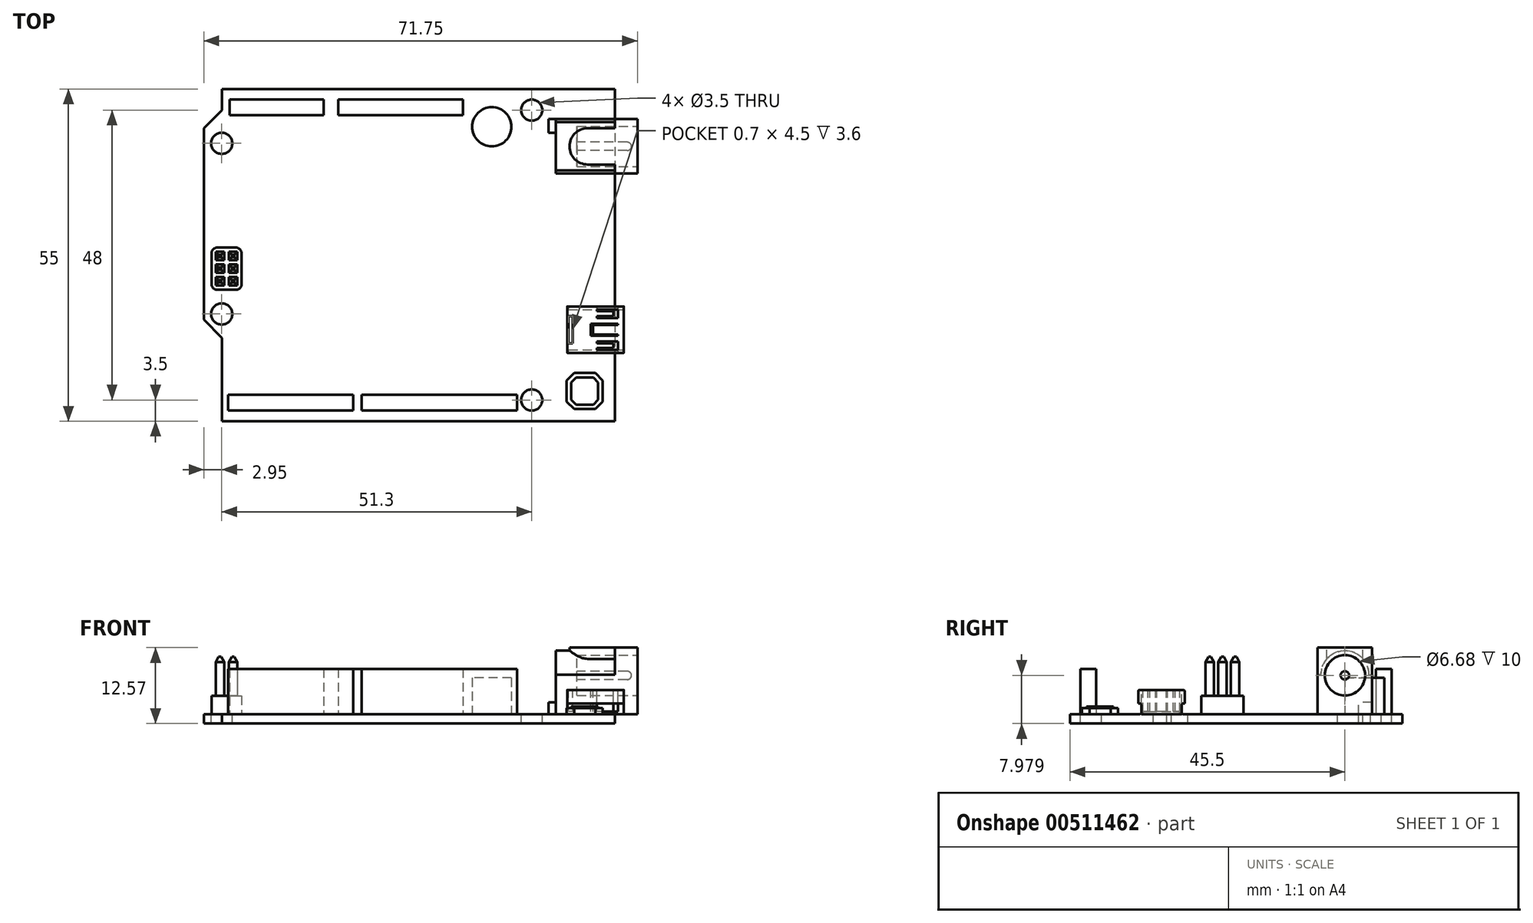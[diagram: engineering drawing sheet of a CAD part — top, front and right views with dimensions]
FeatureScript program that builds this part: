
annotation { "Feature Type Name" : "Feature", "Feature Type Description" : "" }
export const myFeature = defineFeature(function(context is Context, id is Id, definition is map)
    precondition{}
    {
        {
            var Q0;
            Q0=qCreatedBy(makeId("Top.planeOp"),FACE);
            var sketch = newSketch(context, id + "F0", { "sketchPlane" : qUnion([Q0])});
            skLineSegment(sketch, "E0.bottom", {"start": v(32.5, 27.5) * mm, "end": v(-32.5, 27.5) * mm});
            skLineSegment(sketch, "E0.top", {"start": v(32.5, -27.5) * mm, "end": v(-32.5, -27.5) * mm});
            skLineSegment(sketch, "E0.left", {"start": v(32.5, 27.5) * mm, "end": v(32.5, -27.5) * mm});
            skLineSegment(sketch, "E0.right", {"start": v(-32.5, 27.5) * mm, "end": v(-32.5, -27.5) * mm});
            skPoint(sketch, "E0.middle", {"position": v(0, 0) * mm});
            skSolve(sketch);
        }
        {
            var Q0;
            Q0=qSketchRegion(id+"F0",true);
            extrude(context, id + "F1", {"entities" : qUnion([Q0]), "depth" : 1.57 * mm, "offsetDistance" : 25 * mm});
        }
        {
            var Q0;
            Q0=makeQuery(id+"F1.opExtrude","CAP_FACE",FACE,{"disambiguationData":[OSD([sQuery(id+"F0.wireOp",EDGE,"E0.bottom"),sQuery(id+"F0.wireOp",EDGE,"E0.top"),sQuery(id+"F0.wireOp",EDGE,"E0.left"),sQuery(id+"F0.wireOp",EDGE,"E0.right")])],"isStart":false});
            var sketch = newSketch(context, id + "F2", { "sketchPlane" : qUnion([Q0])});
            skLineSegment(sketch, "E1.bottom", {"start": v(-32.5, 24) * mm, "end": v(-35.5, 24) * mm});
            skLineSegment(sketch, "E1.top", {"start": v(-32.5, -13.7) * mm, "end": v(-35.5, -13.7) * mm});
            skLineSegment(sketch, "E1.left", {"start": v(-32.5, 24) * mm, "end": v(-32.5, -13.7) * mm});
            skLineSegment(sketch, "E1.right", {"start": v(-35.5, 24) * mm, "end": v(-35.5, -13.7) * mm});
            skLineSegment(sketch, "E2", {"start": v(-32.5, 24) * mm, "end": v(-35.5, 20.99) * mm});
            skLineSegment(sketch, "E3", {"start": v(-35.5, 5.15) * mm, "end": v(-32.5, 5.15) * mm, "construction": true});
            skLineSegment(sketch, "E4.MirrorCS", {"start": v(-32.5, -13.7) * mm, "end": v(-35.5, -10.69) * mm});
            skSolve(sketch);
        }
        {
            var Q0;
            Q0=makeQuery(id+"F2.imprint","IMPRINT",FACE,{"disambiguationData":[TD([[makeQuery(id+"F2.imprint","IMPRINT",EDGE,{"derivedFrom":sQuery(id+"F2.wireOp",EDGE,"E1.left")}),-1.0]])]});
            var Q1;
            Q1=makeQuery(id+"F1.opExtrude","CAP_FACE",FACE,{"disambiguationData":[OSD([sQuery(id+"F0.wireOp",EDGE,"E0.bottom"),sQuery(id+"F0.wireOp",EDGE,"E0.top"),sQuery(id+"F0.wireOp",EDGE,"E0.left"),sQuery(id+"F0.wireOp",EDGE,"E0.right")])],"isStart":true});
            extrude(context, id + "F3", {"entities" : qUnion([Q0]), "operationType" : NewBodyOperationType.ADD, "endBound" : BoundingType.UP_TO_SURFACE, "oppositeDirection" : true, "depth" : 25 * mm, "endBoundEntityFace" : qUnion([Q1]), "offsetDistance" : 25 * mm});
        }
        {
            var Q0;
            Q0=makeQuery(id+"F3.boolean.opBoolean","MERGE",FACE,{"derivedFrom":[makeQuery(id+"F1.opExtrude","CAP_FACE",FACE,{"disambiguationData":[OSD([sQuery(id+"F0.wireOp",EDGE,"E0.bottom"),sQuery(id+"F0.wireOp",EDGE,"E0.top"),sQuery(id+"F0.wireOp",EDGE,"E0.left"),sQuery(id+"F0.wireOp",EDGE,"E0.right")])],"isStart":false}),makeQuery(id+"F3.opExtrude","CAP_FACE",FACE,{"disambiguationData":[OSD([sQuery(id+"F2.wireOp",EDGE,"E1.left"),sQuery(id+"F2.wireOp",EDGE,"E1.right"),sQuery(id+"F2.wireOp",EDGE,"E2"),sQuery(id+"F2.wireOp",EDGE,"E4.MirrorCS")])],"isStart":true})]});
            var sketch = newSketch(context, id + "F4", { "sketchPlane" : qUnion([Q0])});
            skCircle(sketch, "E5", {"center": v(-32.55, 18.5) * mm, "radius": 1.75 * mm});
            skLineSegment(sketch, "E6", {"start": v(-32.55, 18.5) * mm, "end": v(-32.55, -9.75) * mm, "construction": true});
            skCircle(sketch, "E7", {"center": v(-32.55, -9.75) * mm, "radius": 1.75 * mm});
            skCircle(sketch, "E8", {"center": v(18.75, 24) * mm, "radius": 1.75 * mm});
            skLineSegment(sketch, "E9", {"start": v(18.75, 22.25) * mm, "end": v(18.75, -22.25) * mm, "construction": true});
            skCircle(sketch, "E10", {"center": v(18.75, -24) * mm, "radius": 1.75 * mm});
            skSolve(sketch);
        }
        {
            var Q0;
            Q0=qSketchRegion(id+"F4",true);
            extrude(context, id + "F5", {"entities" : qUnion([Q0]), "operationType" : NewBodyOperationType.REMOVE, "endBound" : BoundingType.THROUGH_ALL, "oppositeDirection" : true, "depth" : 25 * mm, "offsetDistance" : 25 * mm});
        }
        {
            var Q0;
            Q0=makeQuery(id+"F1.opExtrude","SWEPT_FACE",FACE,{"disambiguationData":[OSD([sQuery(id+"F0.wireOp",EDGE,"E0.left")])]});
            var sketch = newSketch(context, id + "F6", { "sketchPlane" : qUnion([Q0])});
            skLineSegment(sketch, "E11.bottom", {"start": v(13.5, 1.57) * mm, "end": v(22.5, 1.57) * mm});
            skLineSegment(sketch, "E11.top", {"start": v(13.5, 12.57) * mm, "end": v(22.5, 12.57) * mm});
            skLineSegment(sketch, "E11.left", {"start": v(13.5, 1.57) * mm, "end": v(13.5, 12.57) * mm});
            skLineSegment(sketch, "E11.right", {"start": v(22.5, 1.57) * mm, "end": v(22.5, 12.57) * mm});
            skSolve(sketch);
        }
        {
            var Q0;
            Q0=qSketchRegion(id+"F6",true);
            extrude(context, id + "F7", {"entities" : qUnion([Q0]), "operationType" : NewBodyOperationType.ADD, "oppositeDirection" : true, "depth" : 11 * mm, "offsetDistance" : 25 * mm, "hasSecondDirection" : true, "secondDirectionOppositeDirection" : false, "secondDirectionDepth" : 3.75 * mm});
        }
        {
            var Q0;
            Q0=makeQuery(id+"F7.opExtrude","SWEPT_FACE",FACE,{"disambiguationData":[OSD([sQuery(id+"F6.wireOp",EDGE,"E11.top")])]});
            var sketch = newSketch(context, id + "F8", { "sketchPlane" : qUnion([Q0])});
            skLineSegment(sketch, "E12.bottom", {"start": v(36.25, 13.5) * mm, "end": v(32.5, 13.5) * mm});
            skLineSegment(sketch, "E12.top", {"start": v(36.25, 22.5) * mm, "end": v(32.5, 22.5) * mm});
            skLineSegment(sketch, "E12.left", {"start": v(36.25, 13.5) * mm, "end": v(36.25, 22.5) * mm});
            skLineSegment(sketch, "E12.right", {"start": v(32.5, 13.5) * mm, "end": v(32.5, 22.5) * mm});
            skLineSegment(sketch, "E13.bottom", {"start": v(32.5, 21) * mm, "end": v(25, 21) * mm});
            skLineSegment(sketch, "E13.top", {"start": v(32.5, 15) * mm, "end": v(25, 15) * mm});
            skLineSegment(sketch, "E13.left", {"start": v(32.5, 21) * mm, "end": v(32.5, 15) * mm});
            skLineSegment(sketch, "E13.right", {"start": v(25, 21) * mm, "end": v(25, 15) * mm});
            skPoint(sketch, "E14", {"position": v(32.5, 18) * mm});
            skLineSegment(sketch, "E15.0", {"start": v(32.5, 27.5) * mm, "end": v(32.5, 22.5) * mm, "construction": true});
            skPoint(sketch, "E16", {"position": v(36.25, 18) * mm});
            skArc(sketch, "E17", {"start": v(28, 21) * mm, "mid": v(25, 18) * mm, "end": v(28, 15) * mm});
            skLineSegment(sketch, "E18", {"start": v(28, 18) * mm, "end": v(25, 18) * mm, "construction": true});
            skPoint(sketch, "E19", {"position": v(25, 18) * mm});
            skLineSegment(sketch, "E20", {"start": v(28, 18) * mm, "end": v(28, 21) * mm, "construction": true});
            skSolve(sketch);
        }
        {
            var Q0;
            {var subQ11=sQuery(id+"F6.wireOp",EDGE,"E11.top");var subQ12=makeQuery(id+"F7.opExtrude","CAP_EDGE",EDGE,{"disambiguationData":[OSD([subQ11])],"isStart":false});Q0=makeQuery(id+"F8.imprint","IMPRINT",FACE,{"disambiguationData":[TD([[makeQuery(id+"F8.imprint","IMPRINT",EDGE,{"derivedFrom":subQ12}),-1.0]])]});}
            var Q1;
            {var subQ0=sQuery(id+"F8.wireOp",EDGE,"E13.right");var subQ1=sQuery(id+"F8.wireOp",EDGE,"E13.bottom");var subQ2=makeQuery(id+"F8.imprint","INTERSECT",VERTEX,{"derivedFrom":[subQ1,subQ0]});Q1=makeQuery(id+"F8.imprint","IMPRINT",FACE,{"disambiguationData":[TD([[makeQuery(id+"F8.imprint","IMPRINT",EDGE,{"disambiguationData":[TD([[subQ2,1.0]])],"derivedFrom":subQ1}),1.0]])]});}
            var Q2;
            {var subQ0=sQuery(id+"F8.wireOp",EDGE,"E13.right");var subQ1=sQuery(id+"F8.wireOp",EDGE,"E13.top");var subQ2=makeQuery(id+"F8.imprint","INTERSECT",VERTEX,{"derivedFrom":[subQ1,subQ0]});Q2=makeQuery(id+"F8.imprint","IMPRINT",FACE,{"disambiguationData":[TD([[makeQuery(id+"F8.imprint","IMPRINT",EDGE,{"disambiguationData":[TD([[subQ2,1.0]])],"derivedFrom":subQ1}),-1.0]])]});}
            extrude(context, id + "F9", {"entities" : qUnion([Q0, Q1, Q2]), "operationType" : NewBodyOperationType.REMOVE, "oppositeDirection" : true, "depth" : 4.5 * mm, "offsetDistance" : 25 * mm});
        }
        {
            var Q0;
            Q0=makeQuery(id+"F7.opExtrude","CAP_FACE",FACE,{"disambiguationData":[OSD([sQuery(id+"F6.wireOp",EDGE,"E11.bottom"),sQuery(id+"F6.wireOp",EDGE,"E11.top"),sQuery(id+"F6.wireOp",EDGE,"E11.left"),sQuery(id+"F6.wireOp",EDGE,"E11.right")])],"isStart":false});
            var sketch = newSketch(context, id + "F10", { "sketchPlane" : qUnion([Q0])});
            skCircle(sketch, "E21", {"center": v(-18, 8.07) * mm, "radius": 4 * mm});
            skPoint(sketch, "E21.centerSnap0", {"position": v(-18, 8.07) * mm});
            skSolve(sketch);
        }
        {
            var Q0;
            Q0=qSketchRegion(id+"F10",true);
            var Q1;
            {var subQ0=sQuery(id+"F8.wireOp",EDGE,"E12.right");Q1=makeQuery(id+"F9.boolean.opBoolean","COPY",FACE,{"derivedFrom":makeQuery(id+"F9.opExtrude","SWEPT_FACE",FACE,{"disambiguationData":[OSD([subQ0]),TDD([makeQuery(id+"F8.imprint","IMPRINT",EDGE,{"disambiguationData":[TD([[makeQuery(id+"F8.imprint","INTERSECT",VERTEX,{"derivedFrom":[subQ0,sQuery(id+"F8.wireOp",EDGE,"E13.top"),sQuery(id+"F8.wireOp",EDGE,"E13.left")]}),1.0]])],"derivedFrom":subQ0})])]})});}
            extrude(context, id + "F11", {"entities" : qUnion([Q0]), "operationType" : NewBodyOperationType.ADD, "endBound" : BoundingType.UP_TO_SURFACE, "oppositeDirection" : true, "depth" : 25 * mm, "endBoundEntityFace" : qUnion([Q1]), "offsetDistance" : 25 * mm});
        }
        {
            var Q0;
            Q0=makeQuery(id+"F7.opExtrude","SWEPT_FACE",FACE,{"disambiguationData":[OSD([sQuery(id+"F6.wireOp",EDGE,"E11.top")])]});
            var sketch = newSketch(context, id + "F12", { "sketchPlane" : qUnion([Q0])});
            skLineSegment(sketch, "E22.0.0", {"start": v(28, 15) * mm, "end": v(32.5, 15) * mm, "construction": true});
            skArc(sketch, "E22.0.1", {"start": v(28, 21) * mm, "mid": v(25, 18) * mm, "end": v(28, 15) * mm, "construction": true});
            skLineSegment(sketch, "E22.0.2", {"start": v(28, 21) * mm, "end": v(32.5, 21) * mm, "construction": true});
            skLineSegment(sketch, "E22.0.3", {"start": v(32.5, 21) * mm, "end": v(32.5, 22) * mm, "construction": true});
            skLineSegment(sketch, "E22.0.4", {"start": v(32.5, 22) * mm, "end": v(21.5, 22) * mm, "construction": true});
            skLineSegment(sketch, "E22.0.5", {"start": v(21.5, 22) * mm, "end": v(21.5, 14) * mm, "construction": true});
            skLineSegment(sketch, "E22.0.6", {"start": v(21.5, 14) * mm, "end": v(32.5, 14) * mm, "construction": true});
            skLineSegment(sketch, "E22.0.7", {"start": v(32.5, 14) * mm, "end": v(32.5, 15) * mm, "construction": true});
            skLineSegment(sketch, "E22.1.0", {"start": v(21.5, 22) * mm, "end": v(32.5, 22) * mm, "construction": true});
            skLineSegment(sketch, "E22.1.1", {"start": v(32.5, 22) * mm, "end": v(32.5, 22.5) * mm, "construction": true});
            skLineSegment(sketch, "E22.1.2", {"start": v(32.5, 22.5) * mm, "end": v(21.5, 22.5) * mm, "construction": true});
            skLineSegment(sketch, "E22.1.3", {"start": v(21.5, 22.5) * mm, "end": v(21.5, 22) * mm, "construction": true});
            skLineSegment(sketch, "E22.2.0", {"start": v(21.5, 14) * mm, "end": v(32.5, 14) * mm, "construction": true});
            skLineSegment(sketch, "E22.2.1", {"start": v(21.5, 14) * mm, "end": v(21.5, 13.5) * mm, "construction": true});
            skLineSegment(sketch, "E22.2.2", {"start": v(21.5, 13.5) * mm, "end": v(32.5, 13.5) * mm, "construction": true});
            skLineSegment(sketch, "E22.2.3", {"start": v(32.5, 13.5) * mm, "end": v(32.5, 14) * mm, "construction": true});
            skLineSegment(sketch, "E23.bottom", {"start": v(21.5, 20.25) * mm, "end": v(22.75, 20.25) * mm});
            skLineSegment(sketch, "E23.top", {"start": v(21.5, 13.5) * mm, "end": v(22.75, 13.5) * mm});
            skLineSegment(sketch, "E23.left", {"start": v(21.5, 20.25) * mm, "end": v(21.5, 13.5) * mm});
            skLineSegment(sketch, "E23.right", {"start": v(22.75, 20.25) * mm, "end": v(22.75, 13.5) * mm});
            skSolve(sketch);
        }
        {
            var Q0;
            Q0=qSketchRegion(id+"F12",true);
            var Q1;
            Q1=makeQuery(id+"F3.boolean.opBoolean","MERGE",FACE,{"derivedFrom":[makeQuery(id+"F1.opExtrude","CAP_FACE",FACE,{"disambiguationData":[OSD([sQuery(id+"F0.wireOp",EDGE,"E0.bottom"),sQuery(id+"F0.wireOp",EDGE,"E0.top"),sQuery(id+"F0.wireOp",EDGE,"E0.left"),sQuery(id+"F0.wireOp",EDGE,"E0.right")])],"isStart":false}),makeQuery(id+"F3.opExtrude","CAP_FACE",FACE,{"disambiguationData":[OSD([sQuery(id+"F2.wireOp",EDGE,"E1.left"),sQuery(id+"F2.wireOp",EDGE,"E1.right"),sQuery(id+"F2.wireOp",EDGE,"E2"),sQuery(id+"F2.wireOp",EDGE,"E4.MirrorCS")])],"isStart":true})]});
            var Q2;
            Q2=makeQuery(id+"F1.opExtrude","SWEPT_BODY",BODY,{"disambiguationData":[OSD([sQuery(id+"F0.wireOp",EDGE,"E0.bottom"),sQuery(id+"F0.wireOp",EDGE,"E0.top"),sQuery(id+"F0.wireOp",EDGE,"E0.left"),sQuery(id+"F0.wireOp",EDGE,"E0.right")])]});
            extrude(context, id + "F13", {"entities" : qUnion([Q0]), "operationType" : NewBodyOperationType.REMOVE, "endBound" : BoundingType.UP_TO_SURFACE, "oppositeDirection" : true, "depth" : 25 * mm, "endBoundEntityFace" : qUnion([Q1]), "endBoundEntityBody" : qUnion([Q2]), "offsetDistance" : 25 * mm});
        }
        {
            var Q0;
            {var subQ1=sQuery(id+"F8.wireOp",EDGE,"E12.right");var subQ2=sQuery(id+"F6.wireOp",EDGE,"E11.right");var subQ3=sQuery(id+"F6.wireOp",EDGE,"E11.top");var subQ4=sQuery(id+"F8.wireOp",EDGE,"E13.bottom");var subQ5=sQuery(id+"F6.wireOp",EDGE,"E11.left");Q0=makeQuery(id+"F11.boolean.opBoolean","SPLIT",FACE,{"disambiguationData":[TD([makeQuery(id+"F7.opExtrude","SWEPT_FACE",FACE,{"disambiguationData":[OSD([subQ2])]})])],"derivedFrom":makeQuery(id+"F9.boolean.opBoolean","COPY",FACE,{"derivedFrom":makeQuery(id+"F9.opExtrude","CAP_FACE",FACE,{"disambiguationData":[OSD([subQ3,subQ5,subQ2,subQ1,subQ4,sQuery(id+"F8.wireOp",EDGE,"E13.top"),sQuery(id+"F8.wireOp",EDGE,"E17")])],"isStart":false})})});}
            var sketch = newSketch(context, id + "F14", { "sketchPlane" : qUnion([Q0])});
            skLineSegment(sketch, "E24.bottom", {"start": v(21.5, 22.5) * mm, "end": v(22.75, 22.5) * mm});
            skLineSegment(sketch, "E24.top", {"start": v(21.5, 20.25) * mm, "end": v(22.75, 20.25) * mm});
            skLineSegment(sketch, "E24.left", {"start": v(21.5, 22.5) * mm, "end": v(21.5, 20.25) * mm});
            skLineSegment(sketch, "E24.right", {"start": v(22.75, 22.5) * mm, "end": v(22.75, 20.25) * mm});
            skPoint(sketch, "E25.0", {"position": v(22.75, 20.25) * mm});
            skSolve(sketch);
        }
        {
            var Q0;
            Q0=qSketchRegion(id+"F14",true);
            var Q1;
            Q1=makeQuery(id+"F1.opExtrude","SWEPT_BODY",BODY,{"disambiguationData":[OSD([sQuery(id+"F0.wireOp",EDGE,"E0.bottom"),sQuery(id+"F0.wireOp",EDGE,"E0.top"),sQuery(id+"F0.wireOp",EDGE,"E0.left"),sQuery(id+"F0.wireOp",EDGE,"E0.right")])]});
            extrude(context, id + "F15", {"entities" : qUnion([Q0]), "operationType" : NewBodyOperationType.REMOVE, "endBound" : BoundingType.THROUGH_ALL, "depth" : 25 * mm, "offsetDistance" : 25 * mm, "hasSecondDirection" : true, "secondDirectionBound" : SecondDirectionBoundingType.UP_TO_BODY, "secondDirectionOppositeDirection" : true, "secondDirectionDepth" : 25 * mm, "secondDirectionBoundEntityBody" : qUnion([Q1]), "hasSecondDirectionOffset" : true, "secondDirectionOffsetDistance" : 3.5 * mm});
        }
        {
            var Q0;
            Q0=makeQuery(id+"F7.opExtrude","CAP_FACE",FACE,{"disambiguationData":[OSD([sQuery(id+"F6.wireOp",EDGE,"E11.bottom"),sQuery(id+"F6.wireOp",EDGE,"E11.top"),sQuery(id+"F6.wireOp",EDGE,"E11.left"),sQuery(id+"F6.wireOp",EDGE,"E11.right")])],"isStart":true});
            var sketch = newSketch(context, id + "F16", { "sketchPlane" : qUnion([Q0])});
            skCircle(sketch, "E26", {"center": v(18, 7.98) * mm, "radius": 3.34 * mm});
            skPoint(sketch, "E26.centerSnap0", {"position": v(18, 12.57) * mm});
            skSolve(sketch);
        }
        {
            var Q0;
            Q0=qSketchRegion(id+"F16",true);
            extrude(context, id + "F17", {"entities" : qUnion([Q0]), "operationType" : NewBodyOperationType.REMOVE, "oppositeDirection" : true, "depth" : 10 * mm, "offsetDistance" : 25 * mm});
        }
        {
            var Q0;
            Q0=makeQuery(id+"F17.boolean.opBoolean","COPY",FACE,{"derivedFrom":makeQuery(id+"F17.opExtrude","CAP_FACE",FACE,{"disambiguationData":[OSD([sQuery(id+"F16.wireOp",EDGE,"E26")])],"isStart":false})});
            var sketch = newSketch(context, id + "F18", { "sketchPlane" : qUnion([Q0])});
            skCircle(sketch, "E27", {"center": v(18, 7.98) * mm, "radius": 0.7 * mm});
            skSolve(sketch);
        }
        {
            var Q0;
            Q0=qSketchRegion(id+"F18",true);
            var Q1;
            Q1=makeQuery(id+"F7.opExtrude","CAP_FACE",FACE,{"disambiguationData":[OSD([sQuery(id+"F6.wireOp",EDGE,"E11.bottom"),sQuery(id+"F6.wireOp",EDGE,"E11.top"),sQuery(id+"F6.wireOp",EDGE,"E11.left"),sQuery(id+"F6.wireOp",EDGE,"E11.right")])],"isStart":true});
            extrude(context, id + "F19", {"entities" : qUnion([Q0]), "operationType" : NewBodyOperationType.ADD, "endBound" : BoundingType.UP_TO_SURFACE, "depth" : 25 * mm, "endBoundEntityFace" : qUnion([Q1]), "hasOffset" : true, "offsetDistance" : 1 * mm});
        }
        {
            var Q0;
            Q0=makeQuery(id+"F19.opExtrude","CAP_EDGE",EDGE,{"disambiguationData":[OSD([sQuery(id+"F18.wireOp",EDGE,"E27")])],"isStart":false});
            fillet(context, id + "F20", {"entities" : qUnion([Q0]), "radius" : 0.7 * mm, "tangentPropagation" : true, "allowEdgeOverflow" : false});
        }
        {
            var Q0;
            Q0=makeQuery(id+"F1.opExtrude","SWEPT_FACE",FACE,{"disambiguationData":[OSD([sQuery(id+"F0.wireOp",EDGE,"E0.left")])]});
            var sketch = newSketch(context, id + "F21", { "sketchPlane" : qUnion([Q0])});
            skLineSegment(sketch, "E28.bottom", {"start": v(-16.2, 1.57) * mm, "end": v(-8.5, 1.57) * mm});
            skLineSegment(sketch, "E28.top", {"start": v(-16.2, 5.57) * mm, "end": v(-8.5, 5.57) * mm});
            skLineSegment(sketch, "E28.left", {"start": v(-16.2, 1.57) * mm, "end": v(-16.2, 5.57) * mm});
            skLineSegment(sketch, "E28.right", {"start": v(-8.5, 1.57) * mm, "end": v(-8.5, 5.57) * mm});
            skSolve(sketch);
        }
        {
            var Q0;
            Q0=makeQuery(id+"F21.imprint","IMPRINT",FACE,{"disambiguationData":[TD([[makeQuery(id+"F21.imprint","IMPRINT",EDGE,{"derivedFrom":sQuery(id+"F21.wireOp",EDGE,"E28.bottom")}),-1.0]])]});
            extrude(context, id + "F22", {"entities" : qUnion([Q0]), "operationType" : NewBodyOperationType.ADD, "oppositeDirection" : true, "depth" : (9.36 - 1.5) * mm, "offsetDistance" : 25 * mm, "hasSecondDirection" : true, "secondDirectionOppositeDirection" : false, "secondDirectionDepth" : 1.5 * mm});
        }
        {
            var Q0;
            Q0=makeQuery(id+"F3.boolean.opBoolean","MERGE",FACE,{"derivedFrom":[makeQuery(id+"F1.opExtrude","CAP_FACE",FACE,{"disambiguationData":[OSD([sQuery(id+"F0.wireOp",EDGE,"E0.bottom"),sQuery(id+"F0.wireOp",EDGE,"E0.top"),sQuery(id+"F0.wireOp",EDGE,"E0.left"),sQuery(id+"F0.wireOp",EDGE,"E0.right")])],"isStart":false}),makeQuery(id+"F3.opExtrude","CAP_FACE",FACE,{"disambiguationData":[OSD([sQuery(id+"F2.wireOp",EDGE,"E1.left"),sQuery(id+"F2.wireOp",EDGE,"E1.right"),sQuery(id+"F2.wireOp",EDGE,"E2"),sQuery(id+"F2.wireOp",EDGE,"E4.MirrorCS")])],"isStart":true})]});
            var sketch = newSketch(context, id + "F23", { "sketchPlane" : qUnion([Q0])});
            skLineSegment(sketch, "E29.bottom", {"start": v(-31.25, 25.75) * mm, "end": v(-15.65, 25.75) * mm});
            skLineSegment(sketch, "E29.top", {"start": v(-31.25, 23.15) * mm, "end": v(-15.65, 23.15) * mm});
            skLineSegment(sketch, "E29.left", {"start": v(-31.25, 25.75) * mm, "end": v(-31.25, 23.15) * mm});
            skLineSegment(sketch, "E29.right", {"start": v(-15.65, 25.75) * mm, "end": v(-15.65, 23.15) * mm});
            skLineSegment(sketch, "E30.bottom", {"start": v(-13.25, 25.75) * mm, "end": v(7.4, 25.75) * mm});
            skLineSegment(sketch, "E30.top", {"start": v(-13.25, 23.15) * mm, "end": v(7.4, 23.15) * mm});
            skLineSegment(sketch, "E30.left", {"start": v(-13.25, 25.75) * mm, "end": v(-13.25, 23.15) * mm});
            skLineSegment(sketch, "E30.right", {"start": v(7.4, 25.75) * mm, "end": v(7.4, 23.15) * mm});
            skLineSegment(sketch, "E31.bottom", {"start": v(-31.5, -23.15) * mm, "end": v(-10.8, -23.15) * mm});
            skLineSegment(sketch, "E31.top", {"start": v(-31.5, -25.75) * mm, "end": v(-10.8, -25.75) * mm});
            skLineSegment(sketch, "E31.left", {"start": v(-31.5, -23.15) * mm, "end": v(-31.5, -25.75) * mm});
            skLineSegment(sketch, "E31.right", {"start": v(-10.8, -23.15) * mm, "end": v(-10.8, -25.75) * mm});
            skLineSegment(sketch, "E32.bottom", {"start": v(-9.4, -23.15) * mm, "end": v(16.35, -23.15) * mm});
            skLineSegment(sketch, "E32.top", {"start": v(-9.4, -25.75) * mm, "end": v(16.35, -25.75) * mm});
            skLineSegment(sketch, "E32.left", {"start": v(-9.4, -23.15) * mm, "end": v(-9.4, -25.75) * mm});
            skLineSegment(sketch, "E32.right", {"start": v(16.35, -23.15) * mm, "end": v(16.35, -25.75) * mm});
            skSolve(sketch);
        }
        {
            var Q0;
            Q0=qSketchRegion(id+"F23",true);
            extrude(context, id + "F24", {"entities" : qUnion([Q0]), "operationType" : NewBodyOperationType.ADD, "depth" : 7.5 * mm, "offsetDistance" : 25 * mm});
        }
        {
            var Q0;
            Q0=makeQuery(id+"F22.opExtrude","SWEPT_FACE",FACE,{"disambiguationData":[OSD([sQuery(id+"F21.wireOp",EDGE,"E28.top")])]});
            var sketch = newSketch(context, id + "F25", { "sketchPlane" : qUnion([Q0])});
            skLineSegment(sketch, "E33.bottom", {"start": v(24.84, -10.1) * mm, "end": v(25.54, -10.1) * mm});
            skLineSegment(sketch, "E33.top", {"start": v(24.84, -14.6) * mm, "end": v(25.54, -14.6) * mm});
            skLineSegment(sketch, "E33.left", {"start": v(24.84, -10.1) * mm, "end": v(24.84, -14.6) * mm});
            skLineSegment(sketch, "E33.right", {"start": v(25.54, -10.1) * mm, "end": v(25.54, -14.6) * mm});
            skLineSegment(sketch, "E34.bottom", {"start": v(28.9, -11.35) * mm, "end": v(33, -11.35) * mm});
            skLineSegment(sketch, "E34.top", {"start": v(28.9, -11.55) * mm, "end": v(33, -11.55) * mm});
            skLineSegment(sketch, "E34.left", {"start": v(28.9, -11.35) * mm, "end": v(28.9, -11.55) * mm});
            skLineSegment(sketch, "E34.right", {"start": v(33, -11.35) * mm, "end": v(33, -11.55) * mm});
            skLineSegment(sketch, "E35.bottom", {"start": v(28.9, -13.15) * mm, "end": v(33, -13.15) * mm});
            skLineSegment(sketch, "E35.top", {"start": v(28.9, -13.35) * mm, "end": v(33, -13.35) * mm});
            skLineSegment(sketch, "E35.left", {"start": v(28.9, -13.15) * mm, "end": v(28.9, -13.35) * mm});
            skLineSegment(sketch, "E35.right", {"start": v(33, -13.15) * mm, "end": v(33, -13.35) * mm});
            skLineSegment(sketch, "E36.bottom", {"start": v(28.9, -13.35) * mm, "end": v(28.5, -13.35) * mm});
            skLineSegment(sketch, "E36.top", {"start": v(28.9, -11.35) * mm, "end": v(28.5, -11.35) * mm});
            skLineSegment(sketch, "E36.left", {"start": v(28.9, -13.35) * mm, "end": v(28.9, -11.35) * mm});
            skLineSegment(sketch, "E36.right", {"start": v(28.5, -13.35) * mm, "end": v(28.5, -11.35) * mm});
            skLineSegment(sketch, "E37", {"start": v(29.5, -9) * mm, "end": v(33, -9) * mm});
            skLineSegment(sketch, "E38", {"start": v(33, -9) * mm, "end": v(33, -10.4) * mm});
            skLineSegment(sketch, "E39", {"start": v(33, -10.4) * mm, "end": v(29.5, -10.4) * mm});
            skLineSegment(sketch, "E40", {"start": v(29.5, -10.4) * mm, "end": v(29.5, -10.1) * mm});
            skLineSegment(sketch, "E41", {"start": v(29.5, -10.1) * mm, "end": v(32.25, -10.1) * mm});
            skLineSegment(sketch, "E42", {"start": v(32.25, -10.1) * mm, "end": v(32.25, -9.3) * mm});
            skLineSegment(sketch, "E43", {"start": v(32.25, -9.3) * mm, "end": v(29.5, -9.3) * mm});
            skLineSegment(sketch, "E44", {"start": v(29.5, -9.3) * mm, "end": v(29.5, -9) * mm});
            skLineSegment(sketch, "E45.0", {"start": v(24.64, -16.2) * mm, "end": v(24.64, -8.5) * mm, "construction": true});
            skLineSegment(sketch, "E45.1", {"start": v(24.64, -8.5) * mm, "end": v(34, -8.5) * mm, "construction": true});
            skPoint(sketch, "E46", {"position": v(24.84, -12.35) * mm});
            skPoint(sketch, "E47", {"position": v(24.64, -12.35) * mm});
            skLineSegment(sketch, "E48", {"start": v(24.84, -12.35) * mm, "end": v(28.5, -12.35) * mm, "construction": true});
            skPoint(sketch, "E49", {"position": v(28.5, -12.35) * mm});
            skLineSegment(sketch, "E50.MirrorCS", {"start": v(29.5, -14.3) * mm, "end": v(29.5, -14.6) * mm});
            skLineSegment(sketch, "E51.MirrorCS", {"start": v(29.5, -15.4) * mm, "end": v(29.5, -15.7) * mm});
            skLineSegment(sketch, "E52.MirrorCS", {"start": v(29.5, -15.7) * mm, "end": v(33, -15.7) * mm});
            skLineSegment(sketch, "E53.MirrorCS", {"start": v(32.25, -15.4) * mm, "end": v(29.5, -15.4) * mm});
            skLineSegment(sketch, "E54.MirrorCS", {"start": v(29.5, -14.6) * mm, "end": v(32.25, -14.6) * mm});
            skLineSegment(sketch, "E55.MirrorCS", {"start": v(33, -14.3) * mm, "end": v(29.5, -14.3) * mm});
            skLineSegment(sketch, "E56.MirrorCS", {"start": v(32.25, -14.6) * mm, "end": v(32.25, -15.4) * mm});
            skLineSegment(sketch, "E57.MirrorCS", {"start": v(33, -15.7) * mm, "end": v(33, -14.3) * mm});
            skSolve(sketch);
        }
        {
            var Q0;
            Q0=makeQuery(id+"F22.opExtrude","CAP_FACE",FACE,{"disambiguationData":[OSD([sQuery(id+"F21.wireOp",EDGE,"E28.bottom"),sQuery(id+"F21.wireOp",EDGE,"E28.top"),sQuery(id+"F21.wireOp",EDGE,"E28.left"),sQuery(id+"F21.wireOp",EDGE,"E28.right")])],"isStart":true});
            var sketch = newSketch(context, id + "F26", { "sketchPlane" : qUnion([Q0])});
            skLineSegment(sketch, "E58.bottom", {"start": v(-16.2, 5.57) * mm, "end": v(-8.5, 5.57) * mm});
            skLineSegment(sketch, "E58.top", {"start": v(-16.2, 3.32) * mm, "end": v(-8.5, 3.32) * mm});
            skLineSegment(sketch, "E58.left", {"start": v(-16.2, 5.57) * mm, "end": v(-16.2, 3.32) * mm});
            skLineSegment(sketch, "E58.right", {"start": v(-8.5, 5.57) * mm, "end": v(-8.5, 3.32) * mm});
            skLineSegment(sketch, "E59.bottom", {"start": v(-12.35, 1.57) * mm, "end": v(-15.7, 1.57) * mm});
            skLineSegment(sketch, "E59.top", {"start": v(-12.35, 3.32) * mm, "end": v(-15.7, 3.32) * mm});
            skLineSegment(sketch, "E59.right", {"start": v(-15.7, 1.57) * mm, "end": v(-15.7, 3.32) * mm});
            skLineSegment(sketch, "E60", {"start": v(-12.35, 3.32) * mm, "end": v(-12.35, 1.57) * mm, "construction": true});
            skLineSegment(sketch, "E61.MirrorCS", {"start": v(-9, 1.57) * mm, "end": v(-9, 3.32) * mm});
            skSolve(sketch);
        }
        {
            var Q0;
            {var subQ3=sQuery(id+"F26.wireOp",EDGE,"E59.right");Q0=makeQuery(id+"F26.imprint","IMPRINT",FACE,{"disambiguationData":[TD([[makeQuery(id+"F26.imprint","IMPRINT",EDGE,{"derivedFrom":subQ3}),1.0]])]});}
            var Q1;
            {var subQ3=sQuery(id+"F26.wireOp",EDGE,"E61.MirrorCS");Q1=makeQuery(id+"F26.imprint","IMPRINT",FACE,{"disambiguationData":[TD([[makeQuery(id+"F26.imprint","IMPRINT",EDGE,{"derivedFrom":subQ3}),-1.0]])]});}
            extrude(context, id + "F27", {"entities" : qUnion([Q0, Q1]), "operationType" : NewBodyOperationType.REMOVE, "endBound" : BoundingType.THROUGH_ALL, "oppositeDirection" : true, "depth" : 25 * mm, "offsetDistance" : 25 * mm});
        }
        {
            var Q0;
            Q0=qSketchRegion(id+"F25",true);
            var Q1;
            {var subQ0=sQuery(id+"F21.wireOp",EDGE,"E28.bottom");var subQ1=makeQuery(id+"F22.opExtrude","CAP_EDGE",EDGE,{"disambiguationData":[OSD([subQ0])],"isStart":true});Q1=makeQuery(id+"F27.boolean.opBoolean","MERGE",FACE,{"derivedFrom":[makeQuery(id+"F13.boolean.opBoolean","MERGE",FACE,{"derivedFrom":[makeQuery(id+"F3.boolean.opBoolean","MERGE",FACE,{"derivedFrom":[makeQuery(id+"F1.opExtrude","CAP_FACE",FACE,{"disambiguationData":[OSD([sQuery(id+"F0.wireOp",EDGE,"E0.bottom"),sQuery(id+"F0.wireOp",EDGE,"E0.top"),sQuery(id+"F0.wireOp",EDGE,"E0.left"),sQuery(id+"F0.wireOp",EDGE,"E0.right")])],"isStart":false}),makeQuery(id+"F3.opExtrude","CAP_FACE",FACE,{"disambiguationData":[OSD([sQuery(id+"F2.wireOp",EDGE,"E1.left"),sQuery(id+"F2.wireOp",EDGE,"E1.right"),sQuery(id+"F2.wireOp",EDGE,"E2"),sQuery(id+"F2.wireOp",EDGE,"E4.MirrorCS")])],"isStart":true})]})],"fromTools":[makeQuery(id+"F13.opExtrude","CAP_FACE",FACE,{"disambiguationData":[OSD([sQuery(id+"F12.wireOp",EDGE,"E23.bottom"),sQuery(id+"F12.wireOp",EDGE,"E23.top"),sQuery(id+"F12.wireOp",EDGE,"E23.left"),sQuery(id+"F12.wireOp",EDGE,"E23.right")])],"isStart":false})]})],"fromTools":[makeQuery(id+"F27.opExtrude","SWEPT_FACE",FACE,{"disambiguationData":[OSD([subQ0]),TDD([makeQuery(id+"F26.imprint","IMPRINT",EDGE,{"disambiguationData":[TD([[makeQuery(id+"F26.imprint","INTERSECT",VERTEX,{"derivedFrom":[subQ1,makeQuery(id+"F22.opExtrude","CAP_EDGE",EDGE,{"disambiguationData":[OSD([sQuery(id+"F21.wireOp",EDGE,"E28.right")])],"isStart":true})]}),-1.0]])],"derivedFrom":subQ1})])]}),makeQuery(id+"F27.opExtrude","SWEPT_FACE",FACE,{"disambiguationData":[OSD([subQ0]),TDD([makeQuery(id+"F26.imprint","IMPRINT",EDGE,{"disambiguationData":[TD([[makeQuery(id+"F26.imprint","INTERSECT",VERTEX,{"derivedFrom":[subQ1,makeQuery(id+"F22.opExtrude","CAP_EDGE",EDGE,{"disambiguationData":[OSD([sQuery(id+"F21.wireOp",EDGE,"E28.left")])],"isStart":true})]}),1.0]])],"derivedFrom":subQ1})])]})]});}
            extrude(context, id + "F28", {"entities" : qUnion([Q0]), "operationType" : NewBodyOperationType.REMOVE, "endBound" : BoundingType.UP_TO_SURFACE, "oppositeDirection" : true, "depth" : 25 * mm, "endBoundEntityFace" : qUnion([Q1]), "hasOffset" : true, "offsetDistance" : 0.4 * mm});
        }
        {
            var Q0;
            Q0=makeQuery(id+"F22.opExtrude","SWEPT_EDGE",EDGE,{"disambiguationData":[OSD([sQuery(id+"F21.wireOp",EDGE,"E28.top"),sQuery(id+"F21.wireOp",EDGE,"E28.right")])]});
            var Q1;
            Q1=makeQuery(id+"F22.opExtrude","SWEPT_EDGE",EDGE,{"disambiguationData":[OSD([sQuery(id+"F21.wireOp",EDGE,"E28.top"),sQuery(id+"F21.wireOp",EDGE,"E28.left")])]});
            var Q2;
            {var subQ0=sQuery(id+"F26.wireOp",EDGE,"E59.right");var subQ1=makeQuery(id+"F27.boolean.opBoolean","COPY",FACE,{"derivedFrom":makeQuery(id+"F27.opExtrude","SWEPT_FACE",FACE,{"disambiguationData":[OSD([subQ0])]})});var subQ2=sQuery(id+"F26.wireOp",EDGE,"E58.top");var subQ3=sQuery(id+"F21.wireOp",EDGE,"E28.left");var subQ4=sQuery(id+"F26.wireOp",EDGE,"E59.top");var subQ5=makeQuery(id+"F27.boolean.opBoolean","COPY",FACE,{"derivedFrom":makeQuery(id+"F27.opExtrude","SWEPT_FACE",FACE,{"disambiguationData":[OSD([subQ2]),TDD([makeQuery(id+"F26.imprint","IMPRINT",EDGE,{"disambiguationData":[TD([[makeQuery(id+"F26.imprint","INTERSECT",VERTEX,{"derivedFrom":[makeQuery(id+"F22.opExtrude","CAP_EDGE",EDGE,{"disambiguationData":[OSD([subQ3])],"isStart":true}),subQ2,sQuery(id+"F26.wireOp",EDGE,"E58.left")]}),-1.0]])],"derivedFrom":subQ2})])]})});Q2=makeQuery(id+"F28.boolean.opBoolean","SPLIT",EDGE,{"disambiguationData":[topologyDisambiguationEdgeConnected([subQ5,subQ1]),TD([makeQuery(id+"F28.opExtrude","SWEPT_FACE",FACE,{"disambiguationData":[OSD([sQuery(id+"F25.wireOp",EDGE,"E57.MirrorCS")])]})])],"derivedFrom":makeQuery(id+"F27.boolean.opBoolean","COPY",EDGE,{"derivedFrom":makeQuery(id+"F27.opExtrude","SWEPT_EDGE",EDGE,{"disambiguationData":[OSD([subQ2,subQ4,subQ0])]})})});}
            var Q3;
            {var subQ0=sQuery(id+"F26.wireOp",EDGE,"E61.MirrorCS");var subQ1=makeQuery(id+"F27.boolean.opBoolean","COPY",FACE,{"derivedFrom":makeQuery(id+"F27.opExtrude","SWEPT_FACE",FACE,{"disambiguationData":[OSD([subQ0])]})});var subQ2=sQuery(id+"F26.wireOp",EDGE,"E58.top");var subQ4=makeQuery(id+"F27.boolean.opBoolean","COPY",FACE,{"derivedFrom":makeQuery(id+"F27.opExtrude","SWEPT_FACE",FACE,{"disambiguationData":[OSD([subQ2]),TDD([makeQuery(id+"F26.imprint","IMPRINT",EDGE,{"disambiguationData":[TD([[makeQuery(id+"F26.imprint","INTERSECT",VERTEX,{"derivedFrom":[subQ2,subQ0]}),-1.0]])],"derivedFrom":subQ2})])]})});Q3=makeQuery(id+"F28.boolean.opBoolean","SPLIT",EDGE,{"disambiguationData":[topologyDisambiguationEdgeConnected([subQ4,subQ1]),TD([makeQuery(id+"F28.opExtrude","SWEPT_FACE",FACE,{"disambiguationData":[OSD([sQuery(id+"F25.wireOp",EDGE,"E38")])]})])],"derivedFrom":makeQuery(id+"F27.boolean.opBoolean","COPY",EDGE,{"derivedFrom":makeQuery(id+"F27.opExtrude","SWEPT_EDGE",EDGE,{"disambiguationData":[OSD([subQ2,subQ0])]})})});}
            var Q4;
            {var subQ0=sQuery(id+"F21.wireOp",EDGE,"E28.bottom");var subQ1=sQuery(id+"F26.wireOp",EDGE,"E59.right");Q4=makeQuery(id+"F27.boolean.opBoolean","COPY",EDGE,{"disambiguationData":[topologyDisambiguationEdgeConnected([makeQuery(id+"F22.opExtrude","SWEPT_FACE",FACE,{"disambiguationData":[OSD([subQ0])]})])],"derivedFrom":makeQuery(id+"F27.opExtrude","SWEPT_EDGE",EDGE,{"disambiguationData":[OSD([subQ0,sQuery(id+"F26.wireOp",EDGE,"E59.bottom"),subQ1])]})});}
            var Q5;
            {var subQ0=sQuery(id+"F21.wireOp",EDGE,"E28.bottom");var subQ1=sQuery(id+"F26.wireOp",EDGE,"E61.MirrorCS");Q5=makeQuery(id+"F27.boolean.opBoolean","COPY",EDGE,{"disambiguationData":[topologyDisambiguationEdgeConnected([makeQuery(id+"F22.opExtrude","SWEPT_FACE",FACE,{"disambiguationData":[OSD([subQ0])]})])],"derivedFrom":makeQuery(id+"F27.opExtrude","SWEPT_EDGE",EDGE,{"disambiguationData":[OSD([subQ0,subQ1])]})});}
            var Q6;
            Q6=makeQuery(id+"F27.boolean.opBoolean","COPY",EDGE,{"derivedFrom":makeQuery(id+"F27.opExtrude","SWEPT_EDGE",EDGE,{"disambiguationData":[OSD([sQuery(id+"F21.wireOp",EDGE,"E28.right"),sQuery(id+"F26.wireOp",EDGE,"E58.top"),sQuery(id+"F26.wireOp",EDGE,"E58.right")])]})});
            var Q7;
            Q7=makeQuery(id+"F27.boolean.opBoolean","COPY",EDGE,{"derivedFrom":makeQuery(id+"F27.opExtrude","SWEPT_EDGE",EDGE,{"disambiguationData":[OSD([sQuery(id+"F21.wireOp",EDGE,"E28.left"),sQuery(id+"F26.wireOp",EDGE,"E58.top"),sQuery(id+"F26.wireOp",EDGE,"E58.left")])]})});
            var Q8;
            Q8=makeQuery(id+"F27.boolean.opBoolean","INTERSECT",EDGE,{"derivedFrom":[makeQuery(id+"F22.opExtrude","CAP_FACE",FACE,{"disambiguationData":[OSD([sQuery(id+"F21.wireOp",EDGE,"E28.bottom"),sQuery(id+"F21.wireOp",EDGE,"E28.top"),sQuery(id+"F21.wireOp",EDGE,"E28.left"),sQuery(id+"F21.wireOp",EDGE,"E28.right")])],"isStart":false}),makeQuery(id+"F27.opExtrude","SWEPT_FACE",FACE,{"disambiguationData":[OSD([sQuery(id+"F26.wireOp",EDGE,"E59.right")])]})]});
            var Q9;
            Q9=makeQuery(id+"F27.boolean.opBoolean","INTERSECT",EDGE,{"derivedFrom":[makeQuery(id+"F22.opExtrude","CAP_FACE",FACE,{"disambiguationData":[OSD([sQuery(id+"F21.wireOp",EDGE,"E28.bottom"),sQuery(id+"F21.wireOp",EDGE,"E28.top"),sQuery(id+"F21.wireOp",EDGE,"E28.left"),sQuery(id+"F21.wireOp",EDGE,"E28.right")])],"isStart":false}),makeQuery(id+"F27.opExtrude","SWEPT_FACE",FACE,{"disambiguationData":[OSD([sQuery(id+"F26.wireOp",EDGE,"E61.MirrorCS")])]})]});
            fillet(context, id + "F29", {"entities" : qUnion([Q0, Q1, Q2, Q3, Q4, Q5, Q6, Q7, Q8, Q9]), "radius" : 0.25 * mm, "tangentPropagation" : true, "allowEdgeOverflow" : false});
        }
        {
            var Q0;
            Q0=makeQuery(id+"F3.boolean.opBoolean","MERGE",FACE,{"derivedFrom":[makeQuery(id+"F1.opExtrude","CAP_FACE",FACE,{"disambiguationData":[OSD([sQuery(id+"F0.wireOp",EDGE,"E0.bottom"),sQuery(id+"F0.wireOp",EDGE,"E0.top"),sQuery(id+"F0.wireOp",EDGE,"E0.left"),sQuery(id+"F0.wireOp",EDGE,"E0.right")])],"isStart":false}),makeQuery(id+"F3.opExtrude","CAP_FACE",FACE,{"disambiguationData":[OSD([sQuery(id+"F2.wireOp",EDGE,"E1.left"),sQuery(id+"F2.wireOp",EDGE,"E1.right"),sQuery(id+"F2.wireOp",EDGE,"E2"),sQuery(id+"F2.wireOp",EDGE,"E4.MirrorCS")])],"isStart":true})]});
            var sketch = newSketch(context, id + "F30", { "sketchPlane" : qUnion([Q0])});
            skLineSegment(sketch, "E62", {"start": v(24.53, -19.53) * mm, "end": v(25.76, -19.53) * mm, "construction": true});
            skLineSegment(sketch, "E63", {"start": v(24.53, -19.53) * mm, "end": v(24.53, -20.76) * mm, "construction": true});
            skLineSegment(sketch, "E64", {"start": v(24.53, -20.76) * mm, "end": v(25.76, -19.53) * mm});
            skCircle(sketch, "E65", {"center": v(27.51, -22.51) * mm, "radius": 4.22 * mm, "construction": true});
            skLineSegment(sketch, "E66", {"start": v(27.51, -22.51) * mm, "end": v(27.51, -18.29) * mm, "construction": true});
            skLineSegment(sketch, "E67", {"start": v(27.51, -22.51) * mm, "end": v(31.74, -22.51) * mm, "construction": true});
            skLineSegment(sketch, "E68.MirrorCS", {"start": v(30.5, -20.76) * mm, "end": v(29.26, -19.53) * mm});
            skLineSegment(sketch, "E69.MirrorCS", {"start": v(30.5, -19.53) * mm, "end": v(29.26, -19.53) * mm, "construction": true});
            skLineSegment(sketch, "E70.MirrorCS", {"start": v(30.5, -19.53) * mm, "end": v(30.5, -20.76) * mm, "construction": true});
            skLineSegment(sketch, "E71.MirrorCS", {"start": v(30.5, -24.26) * mm, "end": v(29.26, -25.5) * mm});
            skLineSegment(sketch, "E72.MirrorCS", {"start": v(24.53, -24.26) * mm, "end": v(25.76, -25.5) * mm});
            skLineSegment(sketch, "E73.MirrorCS", {"start": v(24.53, -25.5) * mm, "end": v(25.76, -25.5) * mm, "construction": true});
            skLineSegment(sketch, "E74.MirrorCS", {"start": v(24.53, -25.5) * mm, "end": v(24.53, -24.26) * mm, "construction": true});
            skLineSegment(sketch, "E75.MirrorCS", {"start": v(30.5, -25.5) * mm, "end": v(29.26, -25.5) * mm, "construction": true});
            skLineSegment(sketch, "E76.MirrorCS", {"start": v(30.5, -25.5) * mm, "end": v(30.5, -24.26) * mm, "construction": true});
            skLineSegment(sketch, "E77", {"start": v(25.76, -19.53) * mm, "end": v(29.26, -19.53) * mm});
            skLineSegment(sketch, "E78", {"start": v(30.5, -20.76) * mm, "end": v(30.5, -24.26) * mm});
            skLineSegment(sketch, "E79", {"start": v(29.26, -25.5) * mm, "end": v(25.76, -25.5) * mm});
            skLineSegment(sketch, "E80", {"start": v(24.53, -24.26) * mm, "end": v(24.53, -20.76) * mm});
            skSolve(sketch);
        }
        {
            var Q0;
            Q0=makeQuery(id+"F30.imprint","IMPRINT",FACE,{"disambiguationData":[TD([[makeQuery(id+"F30.imprint","IMPRINT",EDGE,{"derivedFrom":sQuery(id+"F30.wireOp",EDGE,"E64")}),-1.0]])]});
            extrude(context, id + "F31", {"entities" : qUnion([Q0]), "operationType" : NewBodyOperationType.ADD, "depth" : 1 * mm, "offsetDistance" : 25 * mm});
        }
        {
            var Q0;
            Q0=makeQuery(id+"F31.opExtrude","CAP_FACE",FACE,{"disambiguationData":[OSD([sQuery(id+"F30.wireOp",EDGE,"E64"),sQuery(id+"F30.wireOp",EDGE,"E68.MirrorCS"),sQuery(id+"F30.wireOp",EDGE,"E71.MirrorCS"),sQuery(id+"F30.wireOp",EDGE,"E72.MirrorCS"),sQuery(id+"F30.wireOp",EDGE,"E77"),sQuery(id+"F30.wireOp",EDGE,"E78"),sQuery(id+"F30.wireOp",EDGE,"E79"),sQuery(id+"F30.wireOp",EDGE,"E80")])],"isStart":false});
            var sketch = newSketch(context, id + "F32", { "sketchPlane" : qUnion([Q0])});
            skLineSegment(sketch, "E81.0", {"start": v(24.53, -20.76) * mm, "end": v(25.76, -19.53) * mm, "construction": true});
            skLineSegment(sketch, "E81.1", {"start": v(30.5, -20.76) * mm, "end": v(29.26, -19.53) * mm, "construction": true});
            skLineSegment(sketch, "E81.2", {"start": v(30.5, -24.26) * mm, "end": v(29.26, -25.5) * mm, "construction": true});
            skLineSegment(sketch, "E81.3", {"start": v(24.53, -24.26) * mm, "end": v(25.76, -25.5) * mm, "construction": true});
            skPoint(sketch, "E82.startSnap0", {"position": v(25.14, -20.14) * mm});
            skLineSegment(sketch, "E83", {"start": v(26.07, -20.28) * mm, "end": v(28.95, -20.28) * mm});
            skLineSegment(sketch, "E84", {"start": v(28.95, -20.28) * mm, "end": v(29.75, -21.07) * mm});
            skLineSegment(sketch, "E85", {"start": v(29.75, -21.07) * mm, "end": v(29.75, -23.95) * mm});
            skLineSegment(sketch, "E86", {"start": v(29.75, -23.95) * mm, "end": v(28.95, -24.75) * mm});
            skLineSegment(sketch, "E87", {"start": v(28.95, -24.75) * mm, "end": v(26.07, -24.75) * mm});
            skLineSegment(sketch, "E88", {"start": v(26.07, -24.75) * mm, "end": v(25.28, -23.95) * mm});
            skLineSegment(sketch, "E89", {"start": v(27.51, -19.53) * mm, "end": v(27.51, -25.5) * mm, "construction": true});
            skLineSegment(sketch, "E90", {"start": v(24.53, -22.51) * mm, "end": v(30.5, -22.51) * mm, "construction": true});
            skPoint(sketch, "E91", {"position": v(27.51, -20.28) * mm});
            skPoint(sketch, "E92", {"position": v(29.75, -22.51) * mm});
            skLineSegment(sketch, "E93.MirrorCS", {"start": v(25.28, -23.95) * mm, "end": v(26.07, -24.75) * mm});
            skLineSegment(sketch, "E94.MirrorCS", {"start": v(25.28, -21.07) * mm, "end": v(25.28, -23.95) * mm});
            skLineSegment(sketch, "E95.MirrorCS", {"start": v(26.07, -20.28) * mm, "end": v(25.28, -21.07) * mm});
            skSolve(sketch);
        }
        {
            var Q0;
            Q0=qSketchRegion(id+"F32",true);
            extrude(context, id + "F33", {"entities" : qUnion([Q0]), "operationType" : NewBodyOperationType.ADD, "depth" : 0.25 * mm, "offsetDistance" : 25 * mm});
        }
        {
            var Q0;
            Q0=makeQuery(id+"F3.boolean.opBoolean","MERGE",FACE,{"derivedFrom":[makeQuery(id+"F1.opExtrude","CAP_FACE",FACE,{"disambiguationData":[OSD([sQuery(id+"F0.wireOp",EDGE,"E0.bottom"),sQuery(id+"F0.wireOp",EDGE,"E0.top"),sQuery(id+"F0.wireOp",EDGE,"E0.left"),sQuery(id+"F0.wireOp",EDGE,"E0.right")])],"isStart":false}),makeQuery(id+"F3.opExtrude","CAP_FACE",FACE,{"disambiguationData":[OSD([sQuery(id+"F2.wireOp",EDGE,"E1.left"),sQuery(id+"F2.wireOp",EDGE,"E1.right"),sQuery(id+"F2.wireOp",EDGE,"E2"),sQuery(id+"F2.wireOp",EDGE,"E4.MirrorCS")])],"isStart":true})]});
            var sketch = newSketch(context, id + "F34", { "sketchPlane" : qUnion([Q0])});
            skLineSegment(sketch, "E96.bottom", {"start": v(-34.25, -5.75) * mm, "end": v(-29.25, -5.75) * mm});
            skLineSegment(sketch, "E96.top", {"start": v(-34.25, 1.25) * mm, "end": v(-29.25, 1.25) * mm});
            skLineSegment(sketch, "E96.left", {"start": v(-34.25, -5.75) * mm, "end": v(-34.25, 1.25) * mm});
            skLineSegment(sketch, "E96.right", {"start": v(-29.25, -5.75) * mm, "end": v(-29.25, 1.25) * mm});
            skSolve(sketch);
        }
        {
            var Q0;
            Q0=qSketchRegion(id+"F34",true);
            extrude(context, id + "F35", {"entities" : qUnion([Q0]), "operationType" : NewBodyOperationType.ADD, "depth" : 3 * mm, "offsetDistance" : 25 * mm});
        }
        {
            var Q0;
            Q0=makeQuery(id+"F35.opExtrude","CAP_FACE",FACE,{"disambiguationData":[OSD([sQuery(id+"F34.wireOp",EDGE,"E96.bottom"),sQuery(id+"F34.wireOp",EDGE,"E96.top"),sQuery(id+"F34.wireOp",EDGE,"E96.left"),sQuery(id+"F34.wireOp",EDGE,"E96.right")])],"isStart":false});
            var sketch = newSketch(context, id + "F36", { "sketchPlane" : qUnion([Q0])});
            skLineSegment(sketch, "E97.bottom", {"start": v(-33.55, 0.55) * mm, "end": v(-32.15, 0.55) * mm});
            skLineSegment(sketch, "E97.top", {"start": v(-33.55, -0.85) * mm, "end": v(-32.15, -0.85) * mm});
            skLineSegment(sketch, "E97.left", {"start": v(-33.55, 0.55) * mm, "end": v(-33.55, -0.85) * mm});
            skLineSegment(sketch, "E97.right", {"start": v(-32.15, 0.55) * mm, "end": v(-32.15, -0.85) * mm});
            skLineSegment(sketch, "E98", {"start": v(-31.75, 1.25) * mm, "end": v(-31.75, -5.75) * mm, "construction": true});
            skLineSegment(sketch, "E99.MirrorCS", {"start": v(-29.95, 0.55) * mm, "end": v(-29.95, -0.85) * mm});
            skLineSegment(sketch, "E100.MirrorCS", {"start": v(-29.95, -0.85) * mm, "end": v(-31.35, -0.85) * mm});
            skLineSegment(sketch, "E101.MirrorCS", {"start": v(-31.35, 0.55) * mm, "end": v(-31.35, -0.85) * mm});
            skLineSegment(sketch, "E102.MirrorCS", {"start": v(-29.95, 0.55) * mm, "end": v(-31.35, 0.55) * mm});
            skLineSegment(sketch, "E103.0.1.0", {"start": v(-32.15, -1.55) * mm, "end": v(-32.15, -2.95) * mm});
            skLineSegment(sketch, "E103.0.1.1", {"start": v(-31.35, -1.55) * mm, "end": v(-31.35, -2.95) * mm});
            skLineSegment(sketch, "E103.0.1.2", {"start": v(-29.95, -1.55) * mm, "end": v(-29.95, -2.95) * mm});
            skLineSegment(sketch, "E103.0.1.3", {"start": v(-29.95, -2.95) * mm, "end": v(-31.35, -2.95) * mm});
            skLineSegment(sketch, "E103.0.1.4", {"start": v(-33.55, -1.55) * mm, "end": v(-32.15, -1.55) * mm});
            skLineSegment(sketch, "E103.0.1.5", {"start": v(-29.95, -1.55) * mm, "end": v(-31.35, -1.55) * mm});
            skLineSegment(sketch, "E103.0.1.6", {"start": v(-33.55, -1.55) * mm, "end": v(-33.55, -2.95) * mm});
            skLineSegment(sketch, "E103.0.1.7", {"start": v(-33.55, -2.95) * mm, "end": v(-32.15, -2.95) * mm});
            skLineSegment(sketch, "E103.0.2.0", {"start": v(-32.15, -3.65) * mm, "end": v(-32.15, -5.05) * mm});
            skLineSegment(sketch, "E103.0.2.1", {"start": v(-31.35, -3.65) * mm, "end": v(-31.35, -5.05) * mm});
            skLineSegment(sketch, "E103.0.2.2", {"start": v(-29.95, -3.65) * mm, "end": v(-29.95, -5.05) * mm});
            skLineSegment(sketch, "E103.0.2.3", {"start": v(-29.95, -5.05) * mm, "end": v(-31.35, -5.05) * mm});
            skLineSegment(sketch, "E103.0.2.4", {"start": v(-33.55, -3.65) * mm, "end": v(-32.15, -3.65) * mm});
            skLineSegment(sketch, "E103.0.2.5", {"start": v(-29.95, -3.65) * mm, "end": v(-31.35, -3.65) * mm});
            skLineSegment(sketch, "E103.0.2.6", {"start": v(-33.55, -3.65) * mm, "end": v(-33.55, -5.05) * mm});
            skLineSegment(sketch, "E103.0.2.7", {"start": v(-33.55, -5.05) * mm, "end": v(-32.15, -5.05) * mm});
            skLineSegment(sketch, "E103.direction1", {"start": v(-33.55, -0.85) * mm, "end": v(-8.55, -0.85) * mm, "construction": true});
            skLineSegment(sketch, "E103.direction2", {"start": v(-33.55, -0.85) * mm, "end": v(-33.55, -2.95) * mm, "construction": true});
            skSolve(sketch);
        }
        {
            var Q0;
            Q0=qSketchRegion(id+"F36",true);
            extrude(context, id + "F37", {"entities" : qUnion([Q0]), "operationType" : NewBodyOperationType.ADD, "depth" : 6.5 * mm, "offsetDistance" : 25 * mm});
        }
        {
            var Q0;
            Q0=makeQuery(id+"F37.opExtrude","CAP_EDGE",EDGE,{"disambiguationData":[OSD([sQuery(id+"F36.wireOp",EDGE,"E103.0.2.2")])],"isStart":false});
            var Q1;
            Q1=makeQuery(id+"F37.opExtrude","CAP_EDGE",EDGE,{"disambiguationData":[OSD([sQuery(id+"F36.wireOp",EDGE,"E103.0.2.3")])],"isStart":false});
            var Q2;
            Q2=makeQuery(id+"F37.opExtrude","CAP_EDGE",EDGE,{"disambiguationData":[OSD([sQuery(id+"F36.wireOp",EDGE,"E103.0.1.3")])],"isStart":false});
            var Q3;
            Q3=makeQuery(id+"F37.opExtrude","CAP_EDGE",EDGE,{"disambiguationData":[OSD([sQuery(id+"F36.wireOp",EDGE,"E103.0.1.2")])],"isStart":false});
            var Q4;
            Q4=makeQuery(id+"F37.opExtrude","CAP_EDGE",EDGE,{"disambiguationData":[OSD([sQuery(id+"F36.wireOp",EDGE,"E100.MirrorCS")])],"isStart":false});
            var Q5;
            Q5=makeQuery(id+"F37.opExtrude","CAP_EDGE",EDGE,{"disambiguationData":[OSD([sQuery(id+"F36.wireOp",EDGE,"E99.MirrorCS")])],"isStart":false});
            var Q6;
            Q6=makeQuery(id+"F37.opExtrude","CAP_EDGE",EDGE,{"disambiguationData":[OSD([sQuery(id+"F36.wireOp",EDGE,"E103.0.2.4")])],"isStart":false});
            var Q7;
            Q7=makeQuery(id+"F37.opExtrude","CAP_EDGE",EDGE,{"disambiguationData":[OSD([sQuery(id+"F36.wireOp",EDGE,"E103.0.2.0")])],"isStart":false});
            var Q8;
            Q8=makeQuery(id+"F37.opExtrude","CAP_EDGE",EDGE,{"disambiguationData":[OSD([sQuery(id+"F36.wireOp",EDGE,"E103.0.1.0")])],"isStart":false});
            var Q9;
            Q9=makeQuery(id+"F37.opExtrude","CAP_EDGE",EDGE,{"disambiguationData":[OSD([sQuery(id+"F36.wireOp",EDGE,"E103.0.1.4")])],"isStart":false});
            var Q10;
            Q10=makeQuery(id+"F37.opExtrude","CAP_EDGE",EDGE,{"disambiguationData":[OSD([sQuery(id+"F36.wireOp",EDGE,"E97.right")])],"isStart":false});
            var Q11;
            Q11=makeQuery(id+"F37.opExtrude","CAP_EDGE",EDGE,{"disambiguationData":[OSD([sQuery(id+"F36.wireOp",EDGE,"E97.bottom")])],"isStart":false});
            chamfer(context, id + "F38", {"entities" : qUnion([Q0, Q1, Q2, Q3, Q4, Q5, Q6, Q7, Q8, Q9, Q10, Q11]), "chamferType" : ChamferType.OFFSET_ANGLE, "width" : 0.5 * mm, "oppositeDirection" : true, "angle" : 60 * degree, "tangentPropagation" : true});
        }
        {
            var Q0;
            Q0=makeQuery(id+"F35.opExtrude","SWEPT_EDGE",EDGE,{"disambiguationData":[OSD([sQuery(id+"F34.wireOp",EDGE,"E96.bottom"),sQuery(id+"F34.wireOp",EDGE,"E96.left")])]});
            var Q1;
            Q1=makeQuery(id+"F35.opExtrude","SWEPT_EDGE",EDGE,{"disambiguationData":[OSD([sQuery(id+"F34.wireOp",EDGE,"E96.bottom"),sQuery(id+"F34.wireOp",EDGE,"E96.right")])]});
            var Q2;
            Q2=makeQuery(id+"F35.opExtrude","SWEPT_EDGE",EDGE,{"disambiguationData":[OSD([sQuery(id+"F34.wireOp",EDGE,"E96.top"),sQuery(id+"F34.wireOp",EDGE,"E96.right")])]});
            var Q3;
            Q3=makeQuery(id+"F35.opExtrude","SWEPT_EDGE",EDGE,{"disambiguationData":[OSD([sQuery(id+"F34.wireOp",EDGE,"E96.top"),sQuery(id+"F34.wireOp",EDGE,"E96.left")])]});
            fillet(context, id + "F39", {"entities" : qUnion([Q0, Q1, Q2, Q3]), "radius" : 1 * mm, "tangentPropagation" : true, "allowEdgeOverflow" : false});
        }
        {
            var Q0;
            Q0=makeQuery(id+"F3.boolean.opBoolean","MERGE",FACE,{"derivedFrom":[makeQuery(id+"F1.opExtrude","CAP_FACE",FACE,{"disambiguationData":[OSD([sQuery(id+"F0.wireOp",EDGE,"E0.bottom"),sQuery(id+"F0.wireOp",EDGE,"E0.top"),sQuery(id+"F0.wireOp",EDGE,"E0.left"),sQuery(id+"F0.wireOp",EDGE,"E0.right")])],"isStart":false}),makeQuery(id+"F3.opExtrude","CAP_FACE",FACE,{"disambiguationData":[OSD([sQuery(id+"F2.wireOp",EDGE,"E1.left"),sQuery(id+"F2.wireOp",EDGE,"E1.right"),sQuery(id+"F2.wireOp",EDGE,"E2"),sQuery(id+"F2.wireOp",EDGE,"E4.MirrorCS")])],"isStart":true})]});
            var sketch = newSketch(context, id + "F40", { "sketchPlane" : qUnion([Q0])});
            skCircle(sketch, "E104", {"center": v(12.15, 21.25) * mm, "radius": 3.25 * mm});
            skSolve(sketch);
        }
        {
            var Q0;
            Q0=qSketchRegion(id+"F40",true);
            extrude(context, id + "F41", {"entities" : qUnion([Q0]), "operationType" : NewBodyOperationType.ADD, "depth" : 6 * mm, "offsetDistance" : 25 * mm});
        }
        {
            var Q0;
            Q0=makeQuery(id+"F37.opExtrude","CAP_EDGE",EDGE,{"disambiguationData":[OSD([sQuery(id+"F36.wireOp",EDGE,"E103.0.1.1")])],"isStart":false});
            var Q1;
            Q1=makeQuery(id+"F37.opExtrude","CAP_EDGE",EDGE,{"disambiguationData":[OSD([sQuery(id+"F36.wireOp",EDGE,"E103.0.1.5")])],"isStart":false});
            var Q2;
            Q2=makeQuery(id+"F37.opExtrude","CAP_EDGE",EDGE,{"disambiguationData":[OSD([sQuery(id+"F36.wireOp",EDGE,"E103.0.2.1")])],"isStart":false});
            var Q3;
            Q3=makeQuery(id+"F37.opExtrude","CAP_EDGE",EDGE,{"disambiguationData":[OSD([sQuery(id+"F36.wireOp",EDGE,"E103.0.2.5")])],"isStart":false});
            var Q4;
            Q4=makeQuery(id+"F37.opExtrude","CAP_EDGE",EDGE,{"disambiguationData":[OSD([sQuery(id+"F36.wireOp",EDGE,"E101.MirrorCS")])],"isStart":false});
            var Q5;
            Q5=makeQuery(id+"F37.opExtrude","CAP_EDGE",EDGE,{"disambiguationData":[OSD([sQuery(id+"F36.wireOp",EDGE,"E102.MirrorCS")])],"isStart":false});
            var Q6;
            Q6=makeQuery(id+"F37.opExtrude","CAP_EDGE",EDGE,{"disambiguationData":[OSD([sQuery(id+"F36.wireOp",EDGE,"E97.left")])],"isStart":false});
            var Q7;
            Q7=makeQuery(id+"F37.opExtrude","CAP_EDGE",EDGE,{"disambiguationData":[OSD([sQuery(id+"F36.wireOp",EDGE,"E97.top")])],"isStart":false});
            var Q8;
            Q8=makeQuery(id+"F37.opExtrude","CAP_EDGE",EDGE,{"disambiguationData":[OSD([sQuery(id+"F36.wireOp",EDGE,"E103.0.1.6")])],"isStart":false});
            var Q9;
            Q9=makeQuery(id+"F37.opExtrude","CAP_EDGE",EDGE,{"disambiguationData":[OSD([sQuery(id+"F36.wireOp",EDGE,"E103.0.1.7")])],"isStart":false});
            var Q10;
            Q10=makeQuery(id+"F37.opExtrude","CAP_EDGE",EDGE,{"disambiguationData":[OSD([sQuery(id+"F36.wireOp",EDGE,"E103.0.2.7")])],"isStart":false});
            var Q11;
            Q11=makeQuery(id+"F37.opExtrude","CAP_EDGE",EDGE,{"disambiguationData":[OSD([sQuery(id+"F36.wireOp",EDGE,"E103.0.2.6")])],"isStart":false});
            chamfer(context, id + "F42", {"entities" : qUnion([Q0, Q1, Q2, Q3, Q4, Q5, Q6, Q7, Q8, Q9, Q10, Q11]), "chamferType" : ChamferType.OFFSET_ANGLE, "width" : 0.5 * mm, "oppositeDirection" : false, "angle" : 60 * degree, "tangentPropagation" : true});
        }
    });
